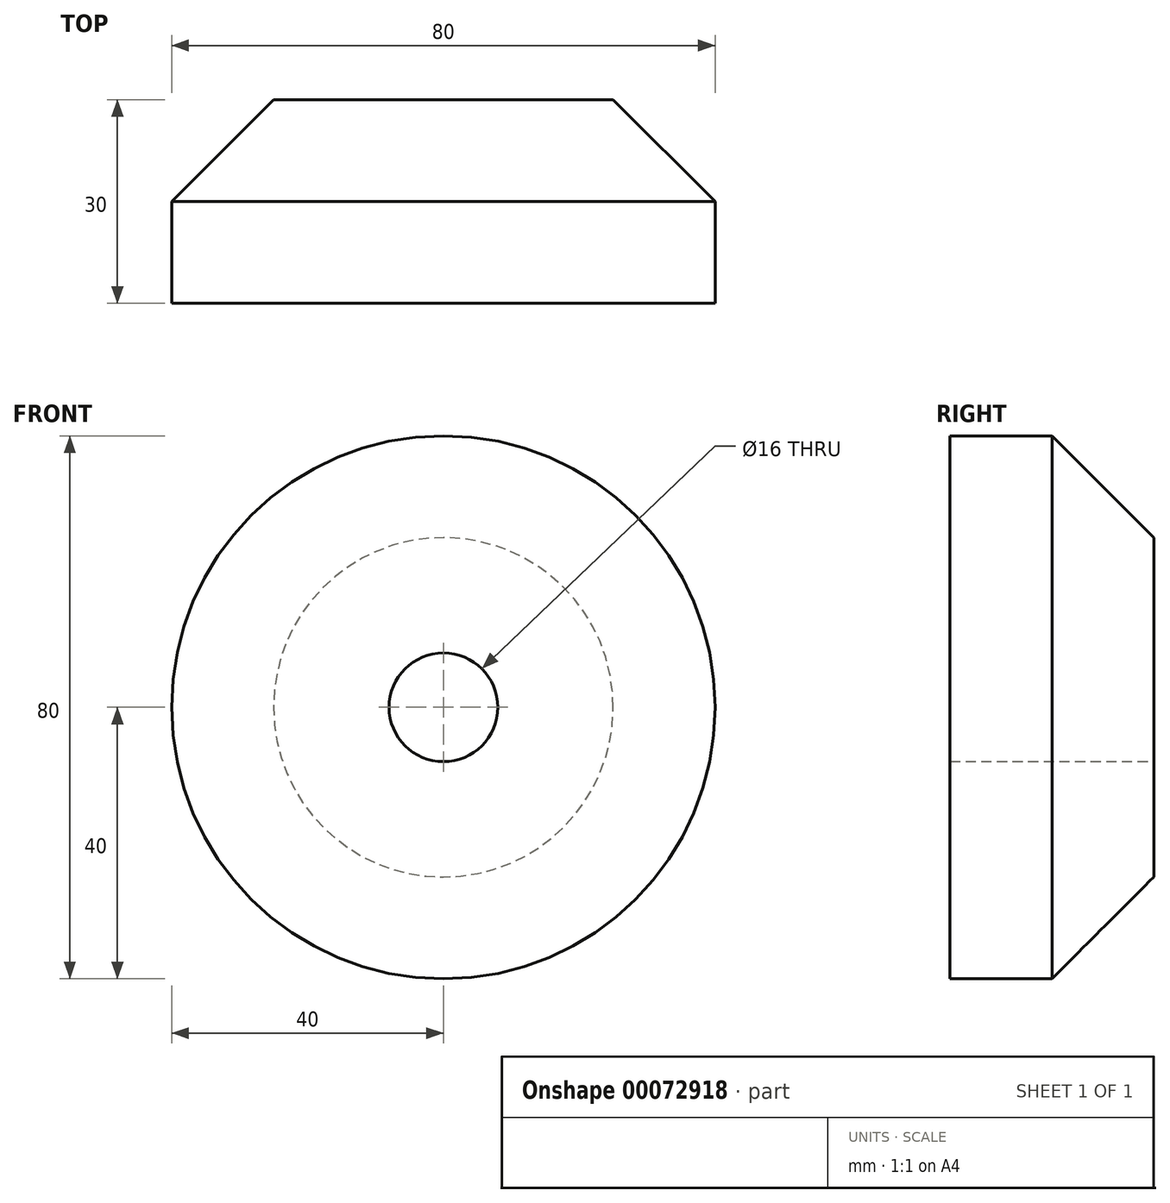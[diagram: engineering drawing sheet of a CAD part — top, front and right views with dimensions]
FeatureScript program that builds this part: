
annotation { "Feature Type Name" : "Feature", "Feature Type Description" : "" }
export const myFeature = defineFeature(function(context is Context, id is Id, definition is map)
    precondition{}
    {
        {
            var Q0;
            Q0=qCreatedBy(makeId("Front.planeOp"),FACE);
            var sketch = newSketch(context, id + "F0", { "sketchPlane" : qUnion([Q0])});
            skCircle(sketch, "E0", {"center": v(0, 0) * mm, "radius": 40 * mm});
            skCircle(sketch, "E1", {"center": v(0, 0) * mm, "radius": 8 * mm});
            skCircle(sketch, "E2", {"center": v(0, 0) * mm, "radius": 25 * mm});
            skSolve(sketch);
        }
        {
            var Q0;
            Q0 = qSketchRegion(id + "F0", true);
            extrude(context, id + "F1", {"entities" : qUnion([Q0]), "depth" : 30 * mm});
        }
        {
            var Q0;
            Q0=makeQuery(id+"F0.imprint","IMPRINT",FACE,{"disambiguationData":[TD([[makeQuery(id+"F0.imprint","IMPRINT",EDGE,{"derivedFrom":sQuery(id+"F0.wireOp",EDGE,"E1")}),-1.0]])]});
            var Q1;
            Q1=makeQuery(id+"F0.imprint","IMPRINT",FACE,{"disambiguationData":[TD([[makeQuery(id+"F0.imprint","IMPRINT",EDGE,{"derivedFrom":sQuery(id+"F0.wireOp",EDGE,"E0")}),1.0]])]});
            extrude(context, id + "F2", {"entities" : qUnion([Q0, Q1]), "operationType" : NewBodyOperationType.ADD, "depth" : 30 * mm});
        }
        {
            var Q0;
            Q0=makeQuery(id+"F1.opExtrude","CAP_EDGE",EDGE,{"disambiguationData":[OSD([sQuery(id+"F0.wireOp",EDGE,"E0")])],"isStart":true});
            chamfer(context, id + "F3", {"entities" : qUnion([Q0]), "width" : 15 * mm, "tangentPropagation" : true});
        }
    });
